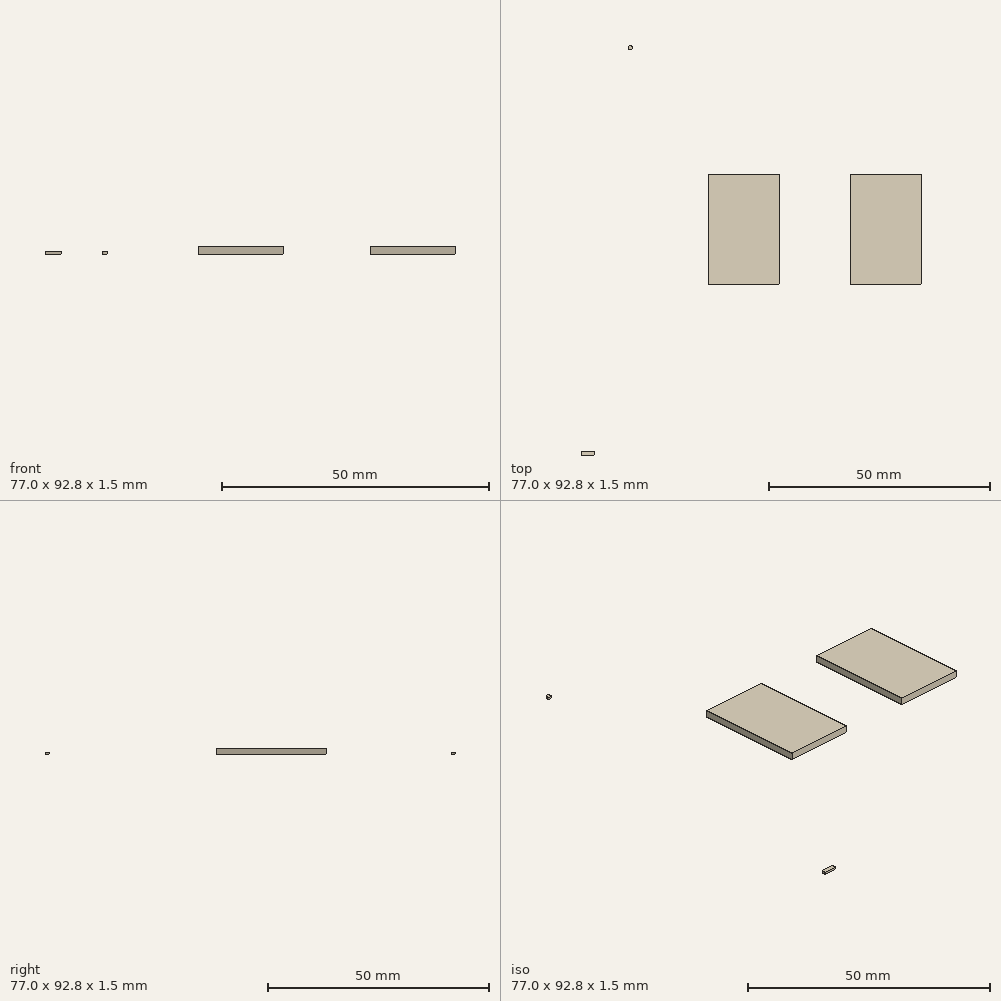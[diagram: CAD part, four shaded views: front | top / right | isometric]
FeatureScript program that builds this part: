
annotation { "Feature Type Name" : "Feature", "Feature Type Description" : "" }
export const myFeature = defineFeature(function(context is Context, id is Id, definition is map)
    precondition{}
    {
        {
            var Q0;
            Q0=qCreatedBy(makeId("Top.planeOp"),FACE);
            var sketch = newSketch(context, id + "F0", { "sketchPlane" : qUnion([Q0])});
            skLineSegment(sketch, "E0.bottom", {"start": v(8.11, 31.85) * mm, "end": v(24.11, 31.85) * mm});
            skLineSegment(sketch, "E0.top", {"start": v(8.11, 6.85) * mm, "end": v(24.11, 6.85) * mm});
            skLineSegment(sketch, "E0.left", {"start": v(8.11, 31.85) * mm, "end": v(8.11, 6.85) * mm});
            skLineSegment(sketch, "E0.right", {"start": v(24.11, 31.85) * mm, "end": v(24.11, 6.85) * mm});
            skLineSegment(sketch, "E1.MirrorCS", {"start": v(-24.11, 31.85) * mm, "end": v(-24.11, 6.85) * mm});
            skLineSegment(sketch, "E2.MirrorCS", {"start": v(-8.11, 31.85) * mm, "end": v(-24.11, 31.85) * mm});
            skLineSegment(sketch, "E3.MirrorCS", {"start": v(-8.11, 6.85) * mm, "end": v(-24.11, 6.85) * mm});
            skLineSegment(sketch, "E4.MirrorCS", {"start": v(-8.11, 31.85) * mm, "end": v(-8.11, 6.85) * mm});
            skSolve(sketch);
        }
        {
            var Q0;
            Q0=makeQuery(id+"F0.imprint","IMPRINT",FACE,{"disambiguationData":[TD([[makeQuery(id+"F0.imprint","IMPRINT",EDGE,{"derivedFrom":sQuery(id+"F0.wireOp",EDGE,"E1.MirrorCS")}),1.0]])]});
            extrude(context, id + "F1", {"entities" : qUnion([Q0]), "depth" : 1.5 * mm});
        }
        {
            var Q0;
            Q0=makeQuery(id+"F0.imprint","IMPRINT",FACE,{"disambiguationData":[TD([[makeQuery(id+"F0.imprint","IMPRINT",EDGE,{"derivedFrom":sQuery(id+"F0.wireOp",EDGE,"E0.bottom")}),-1.0]])]});
            extrude(context, id + "F2", {"entities" : qUnion([Q0]), "depth" : 1.5 * mm});
        }
        {
            var Q0;
            Q0=qCreatedBy(makeId("Top.planeOp"),FACE);
            var sketch = newSketch(context, id + "F3", { "sketchPlane" : qUnion([Q0])});
            skCircle(sketch, "E5", {"center": v(-41.78, 60.53) * mm, "radius": 0.5 * mm});
            skSolve(sketch);
        }
        {
            var Q0;
            Q0=makeQuery(id+"F3.imprint","IMPRINT",FACE,{"disambiguationData":[TD([[makeQuery(id+"F3.imprint","IMPRINT",EDGE,{"derivedFrom":sQuery(id+"F3.wireOp",EDGE,"E5")}),1.0]])]});
            extrude(context, id + "F4", {"entities" : qUnion([Q0]), "depth" : 0.5 * mm});
        }
        {
            var Q0;
            Q0=qCreatedBy(makeId("Top.planeOp"),FACE);
            var sketch = newSketch(context, id + "F5", { "sketchPlane" : qUnion([Q0])});
            skLineSegment(sketch, "E6.bottom", {"start": v(-52.92, -30.78) * mm, "end": v(-49.92, -30.78) * mm});
            skLineSegment(sketch, "E6.top", {"start": v(-52.92, -31.78) * mm, "end": v(-49.92, -31.78) * mm});
            skLineSegment(sketch, "E6.left", {"start": v(-52.92, -30.78) * mm, "end": v(-52.92, -31.78) * mm});
            skLineSegment(sketch, "E6.right", {"start": v(-49.92, -30.78) * mm, "end": v(-49.92, -31.78) * mm});
            skSolve(sketch);
        }
        {
            var Q0;
            Q0=makeQuery(id+"F5.imprint","IMPRINT",FACE,{"disambiguationData":[TD([[makeQuery(id+"F5.imprint","IMPRINT",EDGE,{"derivedFrom":sQuery(id+"F5.wireOp",EDGE,"E6.bottom")}),-1.0]])]});
            extrude(context, id + "F6", {"entities" : qUnion([Q0]), "depth" : 0.5 * mm});
        }
    });
